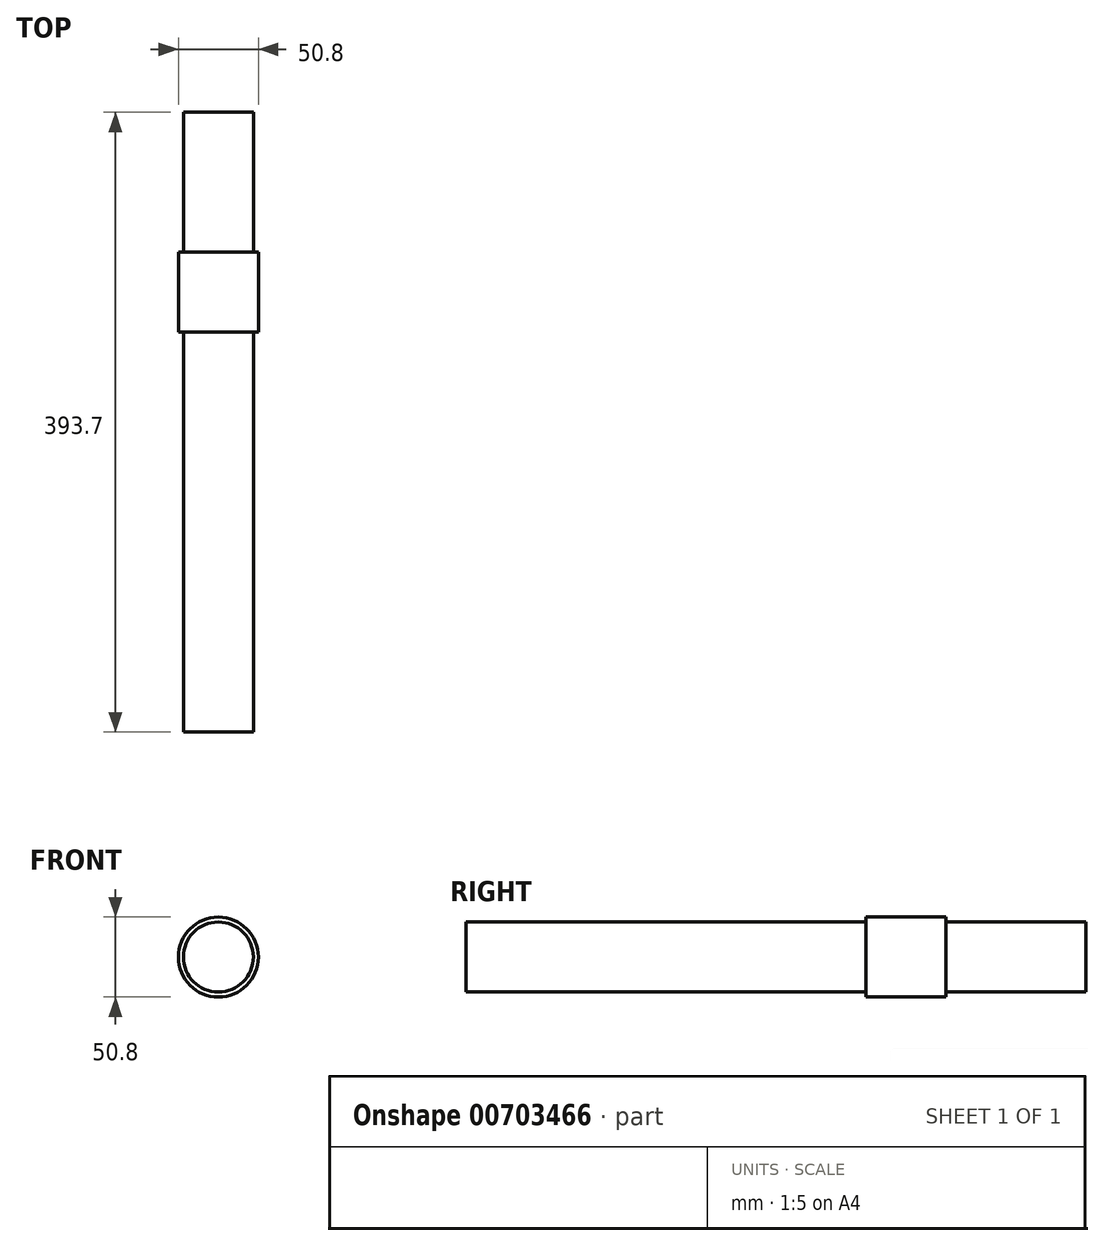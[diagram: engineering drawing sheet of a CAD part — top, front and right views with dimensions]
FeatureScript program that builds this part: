
annotation { "Feature Type Name" : "Feature", "Feature Type Description" : "" }
export const myFeature = defineFeature(function(context is Context, id is Id, definition is map)
    precondition{}
    {
        {
            var Q0;
            Q0=qCreatedBy(makeId("Front.planeOp"),FACE);
            var sketch = newSketch(context, id + "F0", { "sketchPlane" : qUnion([Q0])});
            skCircle(sketch, "E0", {"center": v(0, 0) * mm, "radius": 22.23 * mm});
            skSolve(sketch);
        }
        {
            var Q0;
            Q0 = qSketchRegion(id + "F0", true);
            extrude(context, id + "F1", {"entities" : qUnion([Q0]), "depth" : 406.4 * mm, "offsetDistance" : 25.4 * mm});
        }
        {
            var Q0;
            Q0=makeQuery(id+"F1.opExtrude","CAP_FACE",FACE,{"disambiguationData":[OSD([sQuery(id+"F0.wireOp",EDGE,"E0")])],"isStart":false});
            cPlane(context, id + "F2", {"entities" : qUnion([Q0]), "cplaneType" : CPlaneType.OFFSET, "offset" : 254 * mm, "oppositeDirection" : true, "width" : 152.4 * mm, "height" : 152.4 * mm});
        }
        {
            var Q0;
            Q0=qCreatedBy(id+"F2.planeOp",FACE);
            var sketch = newSketch(context, id + "F3", { "sketchPlane" : qUnion([Q0])});
            skCircle(sketch, "E1", {"center": v(0, 0) * mm, "radius": 25.4 * mm});
            skSolve(sketch);
        }
        {
            var Q0;
            Q0 = qSketchRegion(id + "F3", true);
            extrude(context, id + "F4", {"entities" : qUnion([Q0]), "operationType" : NewBodyOperationType.ADD, "oppositeDirection" : true, "depth" : 50.8 * mm, "offsetDistance" : 25.4 * mm});
        }
        {
            var Q0;
            Q0=makeQuery(id+"F1.opExtrude","CAP_FACE",FACE,{"disambiguationData":[OSD([sQuery(id+"F0.wireOp",EDGE,"E0")])],"isStart":true});
            extrude(context, id + "F5", {"entities" : qUnion([Q0]), "operationType" : NewBodyOperationType.REMOVE, "oppositeDirection" : true, "depth" : 12.7 * mm, "offsetDistance" : 25.4 * mm});
        }
    });
